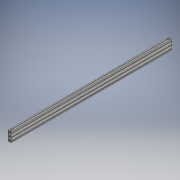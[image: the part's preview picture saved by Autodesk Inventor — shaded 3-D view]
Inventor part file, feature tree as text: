
AUTODESK INVENTOR PART (.ipt)
format: ipt  version: 2018 (Build 220112000, 112)  size: 1,986,560 bytes
history: native  units: in
note: dims shown in document units (in); Inventor stores cm internally (conversion verified against a paired STEP export)
features: other x2, extrude x2, plane x2, mirror x2, sketch x2, direct_edit x1, projected_geometry x1, move_body x1
ambient origin geometry x8: Origin, YZ Plane, XZ Plane, XY Plane, X Axis, Y Axis, Z Axis, Center Point
bodies: Solid1 (feature_tree)
feature tree (13):
  direct_edit  "Direct Edit1"
  other  "Work Axis1"
  extrude  "Extrusion1"  Depth=0.813in
  plane  "Work Plane1"
  mirror  "Mirror1"
  extrude  "Extrusion2"  Depth=0.855in
  plane  "Work Plane3"
  mirror  "Mirror2"
  sketch  "Sketch1"  dims[d0=0.0in d1=0.0in d2=72.0in d3=0.813in]
  projected_geometry  "Projected Loop1"
  sketch  "Sketch2"  dims[d4=0.813in d5=0.855in d6=0.855in d7=0.66in d8=0.0in d9=0.3125in d10=3.0in d11=3.1496in d13=3.0in d14=0.3937in d16=1.0in d18=1.0in d19=0.0in]
  other  "8020-1545-S-1545-S X 145_1_1:1"
  move_body  "Move1"
